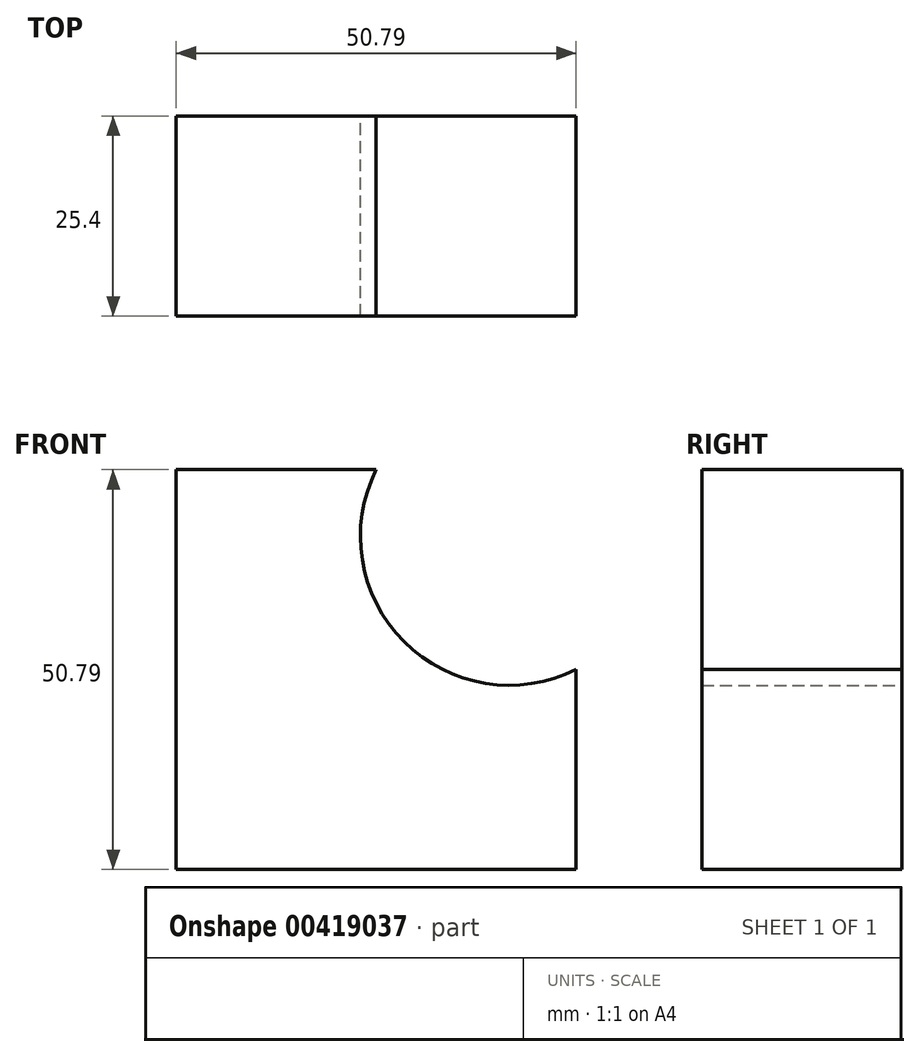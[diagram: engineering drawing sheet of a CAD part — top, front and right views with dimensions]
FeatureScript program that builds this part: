
annotation { "Feature Type Name" : "Feature", "Feature Type Description" : "" }
export const myFeature = defineFeature(function(context is Context, id is Id, definition is map)
    precondition{}
    {
        {
            var Q0;
            Q0=qCreatedBy(makeId("Front.planeOp"),FACE);
            var sketch = newSketch(context, id + "F0", { "sketchPlane" : qUnion([Q0])});
            skLineSegment(sketch, "E0", {"start": v(0, 0) * mm, "end": v(-50.8, 0) * mm});
            skLineSegment(sketch, "E1", {"start": v(-50.8, 0) * mm, "end": v(-50.8, 50.8) * mm});
            skLineSegment(sketch, "E2", {"start": v(-50.8, 50.8) * mm, "end": v(-25.39, 50.8) * mm});
            skLineSegment(sketch, "E3", {"start": v(0, 0) * mm, "end": v(0, 25.4) * mm});
            skArc(sketch, "E4", {"start": v(-25.39, 50.8) * mm, "mid": v(-21.86, 28.94) * mm, "end": v(0, 25.4) * mm});
            skSolve(sketch);
        }
        {
            var Q0;
            Q0=makeQuery(id+"F0.imprint","IMPRINT",FACE,{"disambiguationData":[TD([[makeQuery(id+"F0.imprint","IMPRINT",EDGE,{"derivedFrom":sQuery(id+"F0.wireOp",EDGE,"E0")}),-1.0]])]});
            extrude(context, id + "F1", {"entities" : qUnion([Q0]), "depth" : 25.4 * mm});
        }
    });
